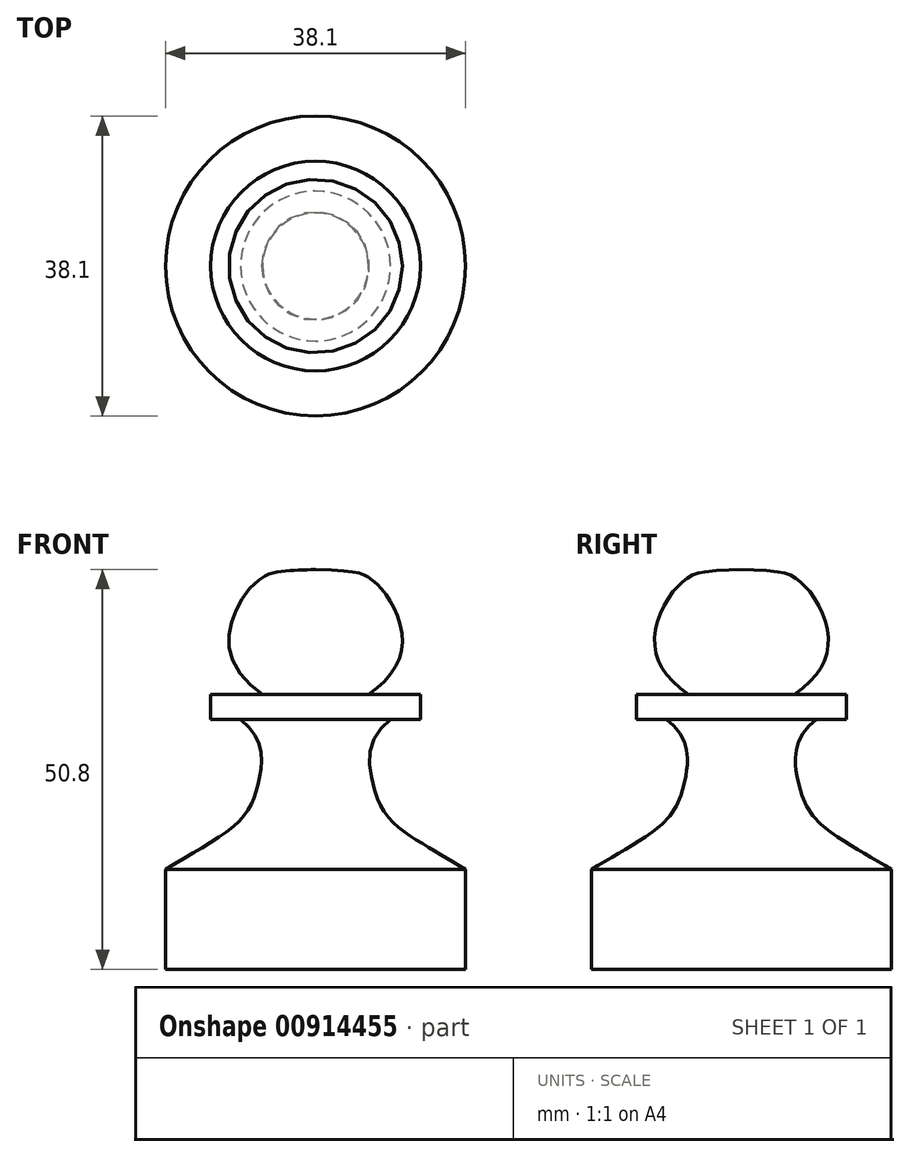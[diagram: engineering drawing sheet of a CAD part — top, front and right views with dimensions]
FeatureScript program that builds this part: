
annotation { "Feature Type Name" : "Feature", "Feature Type Description" : "" }
export const myFeature = defineFeature(function(context is Context, id is Id, definition is map)
    precondition{}
    {
        {
            var Q0;
            Q0=qCreatedBy(makeId("Front.planeOp"),FACE);
            var sketch = newSketch(context, id + "F0", { "sketchPlane" : qUnion([Q0])});
            skLineSegment(sketch, "E0", {"start": v(0, 0) * mm, "end": v(0, 50.8) * mm});
            skLineSegment(sketch, "E1", {"start": v(0, 0) * mm, "end": v(19.05, 0) * mm});
            skLineSegment(sketch, "E2", {"start": v(19.05, 0) * mm, "end": v(19.05, 12.7) * mm});
            skLineSegment(sketch, "E3", {"start": v(0, 31.75) * mm, "end": v(19.05, 31.75) * mm, "construction": true});
            skFitSpline(sketch, "E4", {"points": [v(19.05, 12.7) * mm, v(9.7, 18.82) * mm, v(7.24, 23.73) * mm, v(9.53, 31.75) * mm], "startDerivative": vector(-26.2, 16.38) * mm, "endDerivative": vector(29.14, 21.97) * mm});
            skLineSegment(sketch, "E5.bottom", {"start": v(0, 31.75) * mm, "end": v(13.32, 31.75) * mm});
            skLineSegment(sketch, "E5.top", {"start": v(0, 34.92) * mm, "end": v(13.32, 34.92) * mm});
            skLineSegment(sketch, "E5.left", {"start": v(0, 31.75) * mm, "end": v(0, 34.92) * mm});
            skLineSegment(sketch, "E5.right", {"start": v(13.32, 31.75) * mm, "end": v(13.32, 34.93) * mm});
            skFitSpline(sketch, "E6", {"points": [v(6.73, 34.92) * mm, v(11, 40.93) * mm, v(9.3, 47.1) * mm, v(6.76, 49.77) * mm, v(0, 50.8) * mm], "startDerivative": vector(26.33, 17.94) * mm, "endDerivative": vector(-53.34, 1.9) * mm});
            skSolve(sketch);
        }
        {
            var Q0;
            {var subQ3=sQuery(id+"F0.wireOp",EDGE,"E6");Q0=makeQuery(id+"F0.imprint","IMPRINT",FACE,{"disambiguationData":[TD([[makeQuery(id+"F0.imprint","IMPRINT",EDGE,{"derivedFrom":subQ3}),1.0]])]});}
            var Q1;
            {var subQ7=sQuery(id+"F0.wireOp",EDGE,"E5.right");Q1=makeQuery(id+"F0.imprint","IMPRINT",FACE,{"disambiguationData":[TD([[makeQuery(id+"F0.imprint","IMPRINT",EDGE,{"derivedFrom":subQ7}),1.0]])]});}
            var Q2;
            {var subQ0=sQuery(id+"F0.wireOp",EDGE,"E1");Q2=makeQuery(id+"F0.imprint","IMPRINT",FACE,{"disambiguationData":[TD([[makeQuery(id+"F0.imprint","IMPRINT",EDGE,{"derivedFrom":subQ0}),1.0]])]});}
            var Q3;
            Q3=sQuery(id+"F0.wireOp",EDGE,"E0");
            revolve(context, id + "F1", {"surfaceOperationType" : NewSurfaceOperationType.NEW, "entities" : qUnion([Q0, Q1, Q2]), "axis" : qUnion([Q3]), "revolveType" : RevolveType.FULL});
        }
    });
